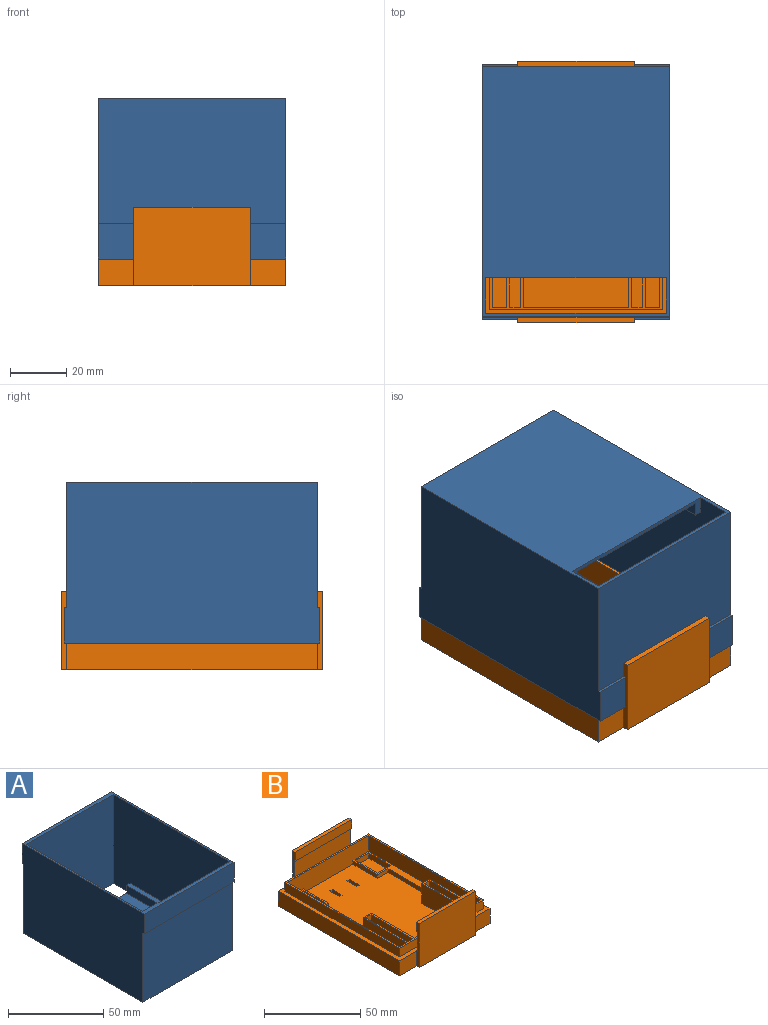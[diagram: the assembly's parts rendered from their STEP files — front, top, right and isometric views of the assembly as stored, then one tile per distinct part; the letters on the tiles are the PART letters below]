
ASSEMBLY  parts=2 mates=1
PART A: 22 faces, bbox 66.7x90.9x57.2 mm
  f0: plane 66.68x44.45mm, normal (0,1,0), area 2963.7mm2, adj f4,f6,f7,f18
  f1: plane 73.66x64.14mm, normal (0,0,1), area 4466.1mm2, adj f2,f9,f10,f11,f12,f13,f15,f16
  f2: plane 86.36x57.15mm, normal (-1,0,0), area 4583.9mm2, adj f1,f3,f7,f8,f10,f11,f13,f14
  f3: plane 90.9x66.68mm, normal (0,0,1), area 522.1mm2, adj f2,f4,f6,f8,f9,f10,f19,f21
  f4: plane 90.9x57.15mm, normal (-1,0,0), area 5106mm2, adj f0,f3,f5,f7,f18,f19,f20,f21
  f5: plane 66.68x44.45mm, normal (0,-1,0), area 2963.9mm2, adj f4,f6,f7,f20
  f6: plane 90.9x57.15mm, normal (1,0,0), area 5106mm2, adj f0,f3,f5,f7,f18,f19,f20,f21
  f7: plane 88.9x66.68mm, normal (0,0,-1), area 5112.9mm2, adj f0,f2,f4,f5,f6,f8,f9,f11
  f8: plane 64.14x57.15mm, normal (0,-1,0), area 3665.3mm2, adj f2,f3,f7,f9
  f9: plane 86.36x57.15mm, normal (1,0,0), area 4583.9mm2, adj f1,f3,f7,f8,f10,f11,f15,f17
  f10: plane 64.14x55.88mm, normal (0,1,0), area 3583.9mm2, adj f1,f2,f3,f9
  f11: plane 64.14x6.35mm, normal (0,1,0), area 107.3mm2, adj f1,f2,f7,f9,f12,f14,f16,f17
  f12: plane 50.8x5.08mm, normal (-1,0,0), area 258.1mm2, adj f1,f11,f13,f14
  f13: plane 5.08x2.54mm, normal (0,-1,0), area 12.9mm2, adj f1,f2,f12,f14
  f14: plane 50.8x2.54mm, normal (0,0,1), area 129mm2, adj f2,f11,f12,f13
  f15: plane 5.08x2.54mm, normal (0,-1,0), area 12.9mm2, adj f1,f9,f16,f17
  f16: plane 50.8x5.08mm, normal (1,0,0), area 258.1mm2, adj f1,f11,f15,f17
  f17: plane 50.8x2.54mm, normal (0,0,1), area 129mm2, adj f9,f11,f15,f16
  f18: plane 66.68x1mm, normal (0,0,-1), area 66.7mm2, adj f0,f4,f6,f19
  f19: plane 66.68x12.7mm, normal (0,1,0), area 846.8mm2, adj f3,f4,f6,f18
  f20: plane 66.68x1mm, normal (0,0,-1), area 66.7mm2, adj f4,f5,f6,f21
  f21: plane 66.68x12.7mm, normal (0,-1,0), area 846.5mm2, adj f3,f4,f6,f20
PART B: 139 faces, bbox 66.7x92.9x27.9 mm
  f0: plane 41.28x5.72mm, normal (0,1,0), area 235.9mm2, adj f1,f107,f108,f110
  f1: plane 27.94x2mm, normal (-1,0,0), area 49.4mm2, adj f0,f8,f10,f11,f108,f109,f110,f111
  f2: plane 12.7x9.53mm, normal (0,-1,0), area 121mm2, adj f8,f10,f12,f107
  f3: plane 41.28x5.72mm, normal (0,-1,0), area 235.9mm2, adj f4,f102,f103,f105
  f4: plane 27.94x2mm, normal (1,0,0), area 49.4mm2, adj f3,f5,f8,f10,f103,f104,f105,f106
  f5: plane 12.7x9.53mm, normal (0,1,0), area 121mm2, adj f4,f8,f10,f12
  f6: plane 61.6x0.01mm, normal (0,0,1), area 0.7mm2, adj f15,f16,f17,f80
  f7: plane 81.82x59.6mm, normal (0,0,1), area 3789.1mm2, adj f18,f19,f20,f22,f23,f24,f25,f26
  f8: plane 89.92x66.68mm, normal (0,0,1), area 805.8mm2, adj f1,f2,f4,f5,f11,f12,f13,f14
  f9: plane 51.06x11.7mm, normal (0,0,1), area 187.7mm2, adj f22,f23,f24,f39,f40,f41,f42,f91
  f10: plane 92.9x66.68mm, normal (0,0,-1), area 6064.9mm2, adj f1,f2,f4,f5,f11,f12,f13,f14
  f11: plane 12.7x9.53mm, normal (0,-1,0), area 121mm2, adj f1,f8,f10,f14
  f12: plane 88.9x9.53mm, normal (1,0,0), area 846.8mm2, adj f2,f5,f8,f10
  f13: plane 12.7x9.53mm, normal (0,1,0), area 121mm2, adj f8,f10,f14,f102
  f14: plane 88.9x9.53mm, normal (-1,0,0), area 846.8mm2, adj f8,f10,f11,f13
  f15: plane 61.6x6.99mm, normal (0,1,0), area 430.2mm2, adj f6,f8,f16,f17
  f16: plane 6.99x0.01mm, normal (-1,0,0), area 0.1mm2, adj f6,f8,f15,f80
  f17: plane 6.99x0.01mm, normal (1,0,0), area 0.1mm2, adj f6,f8,f15,f80
  f18: plane 11.7x2.46mm, normal (0,1,0), area 28.8mm2, adj f7,f19,f21,f72
  f19: plane 18.04x2.46mm, normal (-1,0,0), area 44.4mm2, adj f7,f18,f20,f21
  f20: plane 7.7x2.46mm, normal (0,-1,0), area 18.9mm2, adj f7,f19,f21,f99
  f21: plane 51.06x11.7mm, normal (0,0,1), area 187.7mm2, adj f18,f19,f20,f35,f36,f37,f38,f72
  f22: plane 18.04x2.46mm, normal (1,0,0), area 44.4mm2, adj f7,f9,f23,f24
  f23: plane 11.7x2.46mm, normal (0,1,0), area 28.8mm2, adj f7,f9,f22,f91
  f24: plane 7.7x2.46mm, normal (0,-1,0), area 18.9mm2, adj f7,f9,f22,f97
  f25: plane 2.54x1.91mm, normal (0,1,0), area 4.8mm2, adj f7,f10,f26,f28
  f26: plane 7.24x2.54mm, normal (-1,0,0), area 18.4mm2, adj f7,f10,f25,f27
  f27: plane 2.54x1.91mm, normal (0,-1,0), area 4.8mm2, adj f7,f10,f26,f28
  f28: plane 7.24x2.54mm, normal (1,0,0), area 18.4mm2, adj f7,f10,f25,f27
  f29: plane 7.25x2.54mm, normal (1,0,0), area 18.4mm2, adj f7,f10,f30,f32
  f30: plane 2.54x1.9mm, normal (0,1,0), area 4.8mm2, adj f7,f10,f29,f31
  f31: plane 7.25x2.54mm, normal (-1,0,0), area 18.4mm2, adj f7,f10,f30,f32
  f32: plane 2.54x1.9mm, normal (0,-1,0), area 4.8mm2, adj f7,f10,f29,f31
  f33: plane 81.82x59.6mm, normal (0,0,-1), area 3855.5mm2, adj f35,f36,f37,f38,f39,f40,f41,f42
  f34: plane 81.82x59.6mm, normal (0,0,1), area 4166.7mm2, adj f43,f44,f45,f46,f47,f48,f49,f50
  f35: plane 9.7x3.46mm, normal (0,-1,0), area 33.6mm2, adj f21,f33,f36,f38
  f36: plane 16.04x3.46mm, normal (1,0,0), area 55.5mm2, adj f21,f33,f35,f37
  f37: plane 9.7x3.46mm, normal (0,1,0), area 33.6mm2, adj f21,f33,f36,f38
  f38: plane 16.04x3.46mm, normal (-1,0,0), area 55.5mm2, adj f21,f33,f35,f37
  f39: plane 16.04x3.46mm, normal (-1,0,0), area 55.5mm2, adj f9,f33,f40,f42
  f40: plane 9.7x3.46mm, normal (0,-1,0), area 33.6mm2, adj f9,f33,f39,f41
  f41: plane 16.04x3.46mm, normal (1,0,0), area 55.5mm2, adj f9,f33,f40,f42
  f42: plane 9.7x3.46mm, normal (0,1,0), area 33.6mm2, adj f9,f33,f39,f41
  f43: plane 3.91x0.54mm, normal (0,-1,0), area 2.1mm2, adj f33,f34,f44,f46
  f44: plane 9.24x0.54mm, normal (1,0,0), area 5mm2, adj f33,f34,f43,f45
  f45: plane 3.91x0.54mm, normal (0,1,0), area 2.1mm2, adj f33,f34,f44,f46
  f46: plane 9.24x0.54mm, normal (-1,0,0), area 5mm2, adj f33,f34,f43,f45
  f47: plane 9.25x0.54mm, normal (-1,0,0), area 5mm2, adj f33,f34,f48,f50
  f48: plane 3.9x0.54mm, normal (0,-1,0), area 2.1mm2, adj f33,f34,f47,f49
  f49: plane 9.25x0.54mm, normal (1,0,0), area 5mm2, adj f33,f34,f48,f50
  f50: plane 3.9x0.54mm, normal (0,1,0), area 2.1mm2, adj f33,f34,f47,f49
  f51: plane 5.24x0.54mm, normal (0,1,0), area 2.8mm2, adj f33,f34,f54,f70
  f52: plane 5.87x0.54mm, normal (0,1,0), area 3.2mm2, adj f33,f34,f53,f54
  f53: plane 31.74x0.54mm, normal (-1,0,0), area 17.1mm2, adj f33,f34,f52,f65
  f54: plane 31.74x0.54mm, normal (1,0,0), area 17.1mm2, adj f33,f34,f51,f52
  f55: plane 5.87x0.54mm, normal (0,1,0), area 3.2mm2, adj f33,f34,f56,f57
  f56: plane 31.74x0.54mm, normal (-1,0,0), area 17.1mm2, adj f33,f34,f55,f64
  f57: plane 31.74x0.54mm, normal (1,0,0), area 17.1mm2, adj f33,f34,f55,f65
  f58: plane 59.6x0.54mm, normal (0,-1,0), area 32.2mm2, adj f33,f34,f62,f69
  f59: plane 4x0.54mm, normal (0,1,0), area 2.2mm2, adj f33,f34,f60,f62
  f60: plane 33.02x0.54mm, normal (1,0,0), area 17.8mm2, adj f33,f34,f59,f61
  f61: plane 4x0.54mm, normal (0,-1,0), area 2.2mm2, adj f33,f34,f60,f63
  f62: plane 18.05x0.54mm, normal (1,0,0), area 9.7mm2, adj f33,f34,f58,f59
  f63: plane 30.75x0.54mm, normal (1,0,0), area 16.6mm2, adj f33,f34,f61,f64
  f64: plane 5.24x0.54mm, normal (0,1,0), area 2.8mm2, adj f33,f34,f56,f63
  f65: plane 37.37x0.54mm, normal (0,1,0), area 20.2mm2, adj f33,f34,f53,f57
  f66: plane 33.02x0.54mm, normal (-1,0,0), area 17.8mm2, adj f33,f34,f67,f68
  f67: plane 4x0.54mm, normal (0,1,0), area 2.2mm2, adj f33,f34,f66,f69
  f68: plane 4x0.54mm, normal (0,-1,0), area 2.2mm2, adj f33,f34,f66,f70
  f69: plane 18.05x0.54mm, normal (-1,0,0), area 9.7mm2, adj f33,f34,f58,f67
  f70: plane 30.75x0.54mm, normal (-1,0,0), area 16.6mm2, adj f33,f34,f51,f68
  f71: plane 83.82x5.48mm, normal (1,0,0), area 458.9mm2, adj f8,f80,f82,f84
  f72: plane 81.82x12.46mm, normal (-1,0,0), area 893.9mm2, adj f7,f18,f21,f84,f92,f94,f98
  f73: plane 30.75x12.46mm, normal (-1,0,0), area 383.1mm2, adj f74,f83,f84,f100
  f74: plane 12.46x3.87mm, normal (0,1,0), area 48.3mm2, adj f73,f75,f84,f100
  f75: plane 30.75x12.46mm, normal (1,0,0), area 383.1mm2, adj f74,f83,f84,f100
  f76: plane 30.75x12.46mm, normal (-1,0,0), area 383.1mm2, adj f77,f81,f84,f101
  f77: plane 12.46x3.87mm, normal (0,1,0), area 48.3mm2, adj f76,f78,f84,f101
  f78: plane 30.75x12.46mm, normal (1,0,0), area 383.1mm2, adj f77,f81,f84,f101
  f79: plane 83.82x5.48mm, normal (-1,0,0), area 458.9mm2, adj f8,f80,f82,f84
  f80: plane 61.6x12.46mm, normal (0,-1,0), area 767.5mm2, adj f6,f16,f17,f71,f79,f84
  f81: plane 12.46x3.87mm, normal (0,-1,0), area 48.3mm2, adj f76,f78,f84,f101
  f82: plane 61.6x5.48mm, normal (0,1,0), area 337.2mm2, adj f8,f71,f79,f84
  f83: plane 12.46x3.87mm, normal (0,-1,0), area 48.3mm2, adj f73,f75,f84,f100
  f84: plane 83.82x61.6mm, normal (0,0,1), area 421.4mm2, adj f71,f72,f73,f74,f75,f76,f77,f78
  f85: plane 37.37x12.46mm, normal (0,1,0), area 465.6mm2, adj f7,f84,f87,f90
  f86: plane 12.46x5.24mm, normal (0,1,0), area 65.3mm2, adj f7,f84,f88,f91
  f87: plane 31.74x12.46mm, normal (1,0,0), area 395.5mm2, adj f7,f84,f85,f95
  f88: plane 31.74x12.46mm, normal (-1,0,0), area 395.5mm2, adj f7,f84,f86,f95
  f89: plane 31.74x12.46mm, normal (1,0,0), area 395.5mm2, adj f7,f84,f92,f93
  f90: plane 31.74x12.46mm, normal (-1,0,0), area 395.5mm2, adj f7,f84,f85,f93
  f91: plane 81.82x12.46mm, normal (1,0,0), area 893.9mm2, adj f7,f9,f23,f84,f86,f94,f96
  f92: plane 12.46x5.24mm, normal (0,1,0), area 65.3mm2, adj f7,f72,f84,f89
  f93: plane 12.46x5.87mm, normal (0,1,0), area 73.2mm2, adj f7,f84,f89,f90
  f94: plane 59.6x12.46mm, normal (0,-1,0), area 742.6mm2, adj f7,f72,f84,f91
  f95: plane 12.46x5.87mm, normal (0,1,0), area 73.2mm2, adj f7,f84,f87,f88
  f96: plane 4x2.46mm, normal (0,-1,0), area 9.8mm2, adj f7,f9,f91,f97
  f97: plane 33.02x2.46mm, normal (1,0,0), area 81.2mm2, adj f7,f9,f24,f96
  f98: plane 4x2.46mm, normal (0,-1,0), area 9.8mm2, adj f7,f21,f72,f99
  f99: plane 33.02x2.46mm, normal (-1,0,0), area 81.2mm2, adj f7,f20,f21,f98
  f100: plane 30.75x3.87mm, normal (0,0,1), area 119.1mm2, adj f73,f74,f75,f83
  f101: plane 30.75x3.87mm, normal (0,0,1), area 119.1mm2, adj f76,f77,f78,f81
  f102: plane 27.94x2mm, normal (-1,0,0), area 49.4mm2, adj f3,f8,f10,f13,f103,f104,f105,f106
  f103: plane 41.28x2mm, normal (0,0,1), area 82.6mm2, adj f3,f4,f102,f104
  f104: plane 41.28x27.94mm, normal (0,1,0), area 1153.2mm2, adj f4,f10,f102,f103
  f105: plane 41.28x0.51mm, normal (0,0,-1), area 21mm2, adj f3,f4,f102,f106
  f106: plane 41.28x12.7mm, normal (0,-1,0), area 524.2mm2, adj f4,f8,f102,f105
  f107: plane 27.94x2mm, normal (1,0,0), area 49.4mm2, adj f0,f2,f8,f10,f108,f109,f110,f111
  f108: plane 41.28x2mm, normal (0,0,1), area 82.6mm2, adj f0,f1,f107,f109
  f109: plane 41.28x27.94mm, normal (0,-1,0), area 1153.2mm2, adj f1,f10,f107,f108
  f110: plane 41.28x0.51mm, normal (0,0,-1), area 21mm2, adj f0,f1,f107,f111
  f111: plane 41.28x12.7mm, normal (0,1,0), area 524.2mm2, adj f1,f8,f107,f110
  f112: plane 30.75x3.87mm, normal (0,0,1), area 119.1mm2, adj f113,f114,f115,f116
  f113: plane 3.87x0.54mm, normal (0,-1,0), area 2.1mm2, adj f112,f114,f116,f117
  f114: plane 30.75x0.54mm, normal (1,0,0), area 16.6mm2, adj f112,f113,f115,f117
  f115: plane 3.87x0.54mm, normal (0,1,0), area 2.1mm2, adj f112,f114,f116,f117
  f116: plane 30.75x0.54mm, normal (-1,0,0), area 16.6mm2, adj f112,f113,f115,f117
  f117: plane 30.75x3.87mm, normal (0,0,-1), area 119.1mm2, adj f113,f114,f115,f116
  f118: plane 61.6x0.54mm, normal (0,1,0), area 33.3mm2, adj f119,f121,f126,f132
  f119: plane 83.82x0.54mm, normal (1,0,0), area 45.3mm2, adj f118,f120,f126,f132
  f120: plane 61.6x0.54mm, normal (0,-1,0), area 33.3mm2, adj f119,f121,f126,f132
  f121: plane 83.82x0.54mm, normal (-1,0,0), area 45.3mm2, adj f118,f120,f126,f132
  f122: plane 85.82x6.99mm, normal (1,0,0), area 599.5mm2, adj f123,f125,f126,f127
  f123: plane 63.6x6.99mm, normal (0,1,0), area 444.2mm2, adj f122,f124,f126,f127
  f124: plane 85.82x6.99mm, normal (-1,0,0), area 599.5mm2, adj f123,f125,f126,f127
  f125: plane 63.6x6.99mm, normal (0,-1,0), area 444.2mm2, adj f122,f124,f126,f127
  f126: plane 85.82x63.6mm, normal (0,0,-1), area 294.8mm2, adj f118,f119,f120,f121,f122,f123,f124,f125
  f127: plane 86.9x64.68mm, normal (0,0,-1), area 162.5mm2, adj f122,f123,f124,f125,f128,f129,f130,f131
  f128: plane 86.9x7.53mm, normal (1,0,0), area 653.9mm2, adj f127,f129,f131,f132
  f129: plane 64.68x7.53mm, normal (0,-1,0), area 486.7mm2, adj f127,f128,f130,f132
  f130: plane 86.9x7.53mm, normal (-1,0,0), area 653.9mm2, adj f127,f129,f131,f132
  f131: plane 64.68x7.53mm, normal (0,1,0), area 486.7mm2, adj f127,f128,f130,f132
  f132: plane 86.9x64.68mm, normal (0,0,1), area 457.4mm2, adj f118,f119,f120,f121,f128,f129,f130,f131
  f133: plane 30.75x3.87mm, normal (0,0,1), area 119.1mm2, adj f134,f135,f136,f137
  f134: plane 3.87x0.54mm, normal (0,-1,0), area 2.1mm2, adj f133,f135,f137,f138
  f135: plane 30.75x0.54mm, normal (1,0,0), area 16.6mm2, adj f133,f134,f136,f138
  f136: plane 3.87x0.54mm, normal (0,1,0), area 2.1mm2, adj f133,f135,f137,f138
  f137: plane 30.75x0.54mm, normal (-1,0,0), area 16.6mm2, adj f133,f134,f136,f138
  f138: plane 30.75x3.87mm, normal (0,0,-1), area 119.1mm2, adj f134,f135,f136,f137
PLACE A rot(axis=(1,0,0),180deg) t=(1.41,10.82,52.4)mm
PLACE B t=(0.28,-10.2,-14.27)mm
MATE fastened A.f3 <-> B.f8  axis (0,0,-1) through (-33.05,-0.04,-4.75)mm
